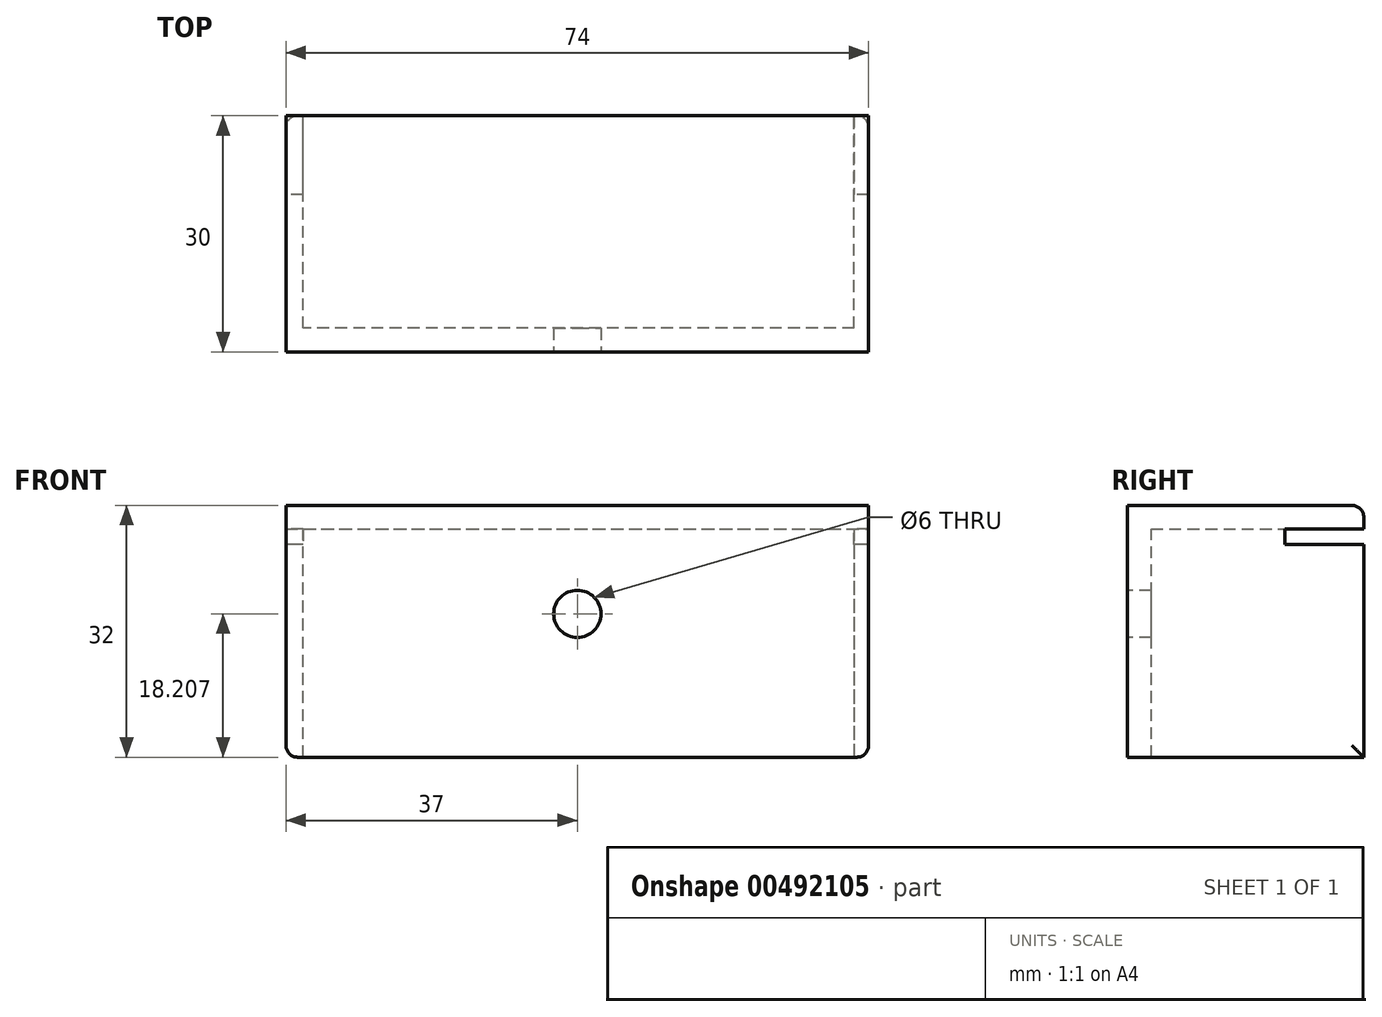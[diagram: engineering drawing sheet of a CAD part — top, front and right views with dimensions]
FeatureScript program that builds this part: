
annotation { "Feature Type Name" : "Feature", "Feature Type Description" : "" }
export const myFeature = defineFeature(function(context is Context, id is Id, definition is map)
    precondition{}
    {
        {
            var Q0;
            Q0=qCreatedBy(makeId("Front.planeOp"),FACE);
            var sketch = newSketch(context, id + "F0", { "sketchPlane" : qUnion([Q0])});
            skLineSegment(sketch, "E0", {"start": v(0, 0) * mm, "end": v(37, 0) * mm});
            skLineSegment(sketch, "E1", {"start": v(0, 0) * mm, "end": v(-37, 0) * mm});
            skLineSegment(sketch, "E2", {"start": v(-37, 0) * mm, "end": v(-37, 32) * mm});
            skLineSegment(sketch, "E3", {"start": v(-37, 32) * mm, "end": v(37, 32) * mm});
            skLineSegment(sketch, "E4", {"start": v(37, 32) * mm, "end": v(37, 0) * mm});
            skSolve(sketch);
        }
        {
            var Q0;
            Q0=makeQuery(id+"F0.imprint","IMPRINT",FACE,{"disambiguationData":[TD([[makeQuery(id+"F0.imprint","IMPRINT",EDGE,{"derivedFrom":sQuery(id+"F0.wireOp",EDGE,"E0")}),1.0]])]});
            var sketch = newSketch(context, id + "F1", { "sketchPlane" : qUnion([Q0])});
            skLineSegment(sketch, "E5", {"start": v(-34.84, 0) * mm, "end": v(-34.84, 29) * mm});
            skLineSegment(sketch, "E6", {"start": v(-34.84, 29) * mm, "end": v(35.16, 29) * mm});
            skLineSegment(sketch, "E7", {"start": v(35.16, 29) * mm, "end": v(35.16, 0) * mm});
            skSolve(sketch);
        }
        {
            var Q0;
            Q0=makeQuery(id+"F0.imprint","IMPRINT",FACE,{"disambiguationData":[TD([[makeQuery(id+"F0.imprint","IMPRINT",EDGE,{"derivedFrom":sQuery(id+"F0.wireOp",EDGE,"E0")}),1.0]])]});
            extrude(context, id + "F2", {"entities" : qUnion([Q0]), "depth" : 30 * mm});
        }
        {
            var Q0;
            {var subQ4=sQuery(id+"F1.wireOp",EDGE,"E5");Q0=makeQuery(id+"F1.imprint","IMPRINT",FACE,{"disambiguationData":[TD([[makeQuery(id+"F1.imprint","IMPRINT",EDGE,{"derivedFrom":subQ4}),-1.0]])]});}
            extrude(context, id + "F3", {"entities" : qUnion([Q0]), "operationType" : NewBodyOperationType.REMOVE, "depth" : 27 * mm});
        }
        {
            var Q0;
            Q0=makeQuery(id+"F2.opExtrude","SWEPT_FACE",FACE,{"disambiguationData":[OSD([sQuery(id+"F0.wireOp",EDGE,"E2")])]});
            var sketch = newSketch(context, id + "F4", { "sketchPlane" : qUnion([Q0])});
            skLineSegment(sketch, "E8", {"start": v(0, 29) * mm, "end": v(10, 29) * mm});
            skLineSegment(sketch, "E9", {"start": v(10, 29) * mm, "end": v(10, 27) * mm});
            skLineSegment(sketch, "E10", {"start": v(10, 27) * mm, "end": v(0, 27) * mm});
            skSolve(sketch);
        }
        {
            var Q0;
            {var subQ0=sQuery(id+"F4.wireOp",EDGE,"E8");Q0=makeQuery(id+"F4.imprint","IMPRINT",FACE,{"disambiguationData":[TD([[makeQuery(id+"F4.imprint","IMPRINT",EDGE,{"derivedFrom":subQ0}),-1.0]])]});}
            extrude(context, id + "F5", {"entities" : qUnion([Q0]), "operationType" : NewBodyOperationType.REMOVE, "oppositeDirection" : true, "depth" : 74.5 * mm});
        }
        {
            var Q0;
            Q0=makeQuery(id+"F2.opExtrude","CAP_FACE",FACE,{"disambiguationData":[OSD([sQuery(id+"F0.wireOp",EDGE,"E0"),sQuery(id+"F0.wireOp",EDGE,"E1"),sQuery(id+"F0.wireOp",EDGE,"E2"),sQuery(id+"F0.wireOp",EDGE,"E3"),sQuery(id+"F0.wireOp",EDGE,"E4")])],"isStart":false});
            var sketch = newSketch(context, id + "F6", { "sketchPlane" : qUnion([Q0])});
            skCircle(sketch, "E11", {"center": v(0, 18.2) * mm, "radius": 3 * mm});
            skSolve(sketch);
        }
        {
            var Q0;
            Q0=makeQuery(id+"F6.imprint","IMPRINT",FACE,{"disambiguationData":[TD([[makeQuery(id+"F6.imprint","IMPRINT",EDGE,{"derivedFrom":sQuery(id+"F6.wireOp",EDGE,"E11")}),1.0]])]});
            extrude(context, id + "F7", {"entities" : qUnion([Q0]), "operationType" : NewBodyOperationType.REMOVE, "oppositeDirection" : true, "depth" : 25 * mm});
        }
        {
            var Q0;
            Q0=makeQuery(id+"F2.opExtrude","SWEPT_EDGE",EDGE,{"disambiguationData":[OSD([sQuery(id+"F0.wireOp",EDGE,"E0"),sQuery(id+"F0.wireOp",EDGE,"E4")])]});
            var Q1;
            Q1=makeQuery(id+"F2.opExtrude","CAP_EDGE",EDGE,{"disambiguationData":[OSD([sQuery(id+"F0.wireOp",EDGE,"E3")])],"isStart":true});
            var Q2;
            Q2=makeQuery(id+"F2.opExtrude","SWEPT_EDGE",EDGE,{"disambiguationData":[OSD([sQuery(id+"F0.wireOp",EDGE,"E1"),sQuery(id+"F0.wireOp",EDGE,"E2")])]});
            var Q3;
            {var subQ2=sQuery(id+"F0.wireOp",EDGE,"E2");Q3=makeQuery(id+"F5.boolean.opBoolean","SPLIT",EDGE,{"disambiguationData":[TD([makeQuery(id+"F5.opExtrude","SWEPT_FACE",FACE,{"disambiguationData":[OSD([sQuery(id+"F4.wireOp",EDGE,"E10")])]})])],"derivedFrom":makeQuery(id+"F2.opExtrude","CAP_EDGE",EDGE,{"disambiguationData":[OSD([subQ2])],"isStart":true})});}
            var Q4;
            {var subQ2=sQuery(id+"F0.wireOp",EDGE,"E4");Q4=makeQuery(id+"F5.boolean.opBoolean","SPLIT",EDGE,{"disambiguationData":[TD([makeQuery(id+"F5.opExtrude","SWEPT_FACE",FACE,{"disambiguationData":[OSD([sQuery(id+"F4.wireOp",EDGE,"E10")])]})])],"derivedFrom":makeQuery(id+"F2.opExtrude","CAP_EDGE",EDGE,{"disambiguationData":[OSD([subQ2])],"isStart":true})});}
            fillet(context, id + "F8", {"entities" : qUnion([Q0, Q1, Q2, Q3, Q4]), "radius" : 1.5 * mm, "tangentPropagation" : true, "allowEdgeOverflow" : false});
        }
    });
